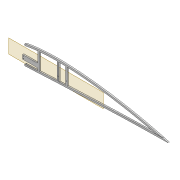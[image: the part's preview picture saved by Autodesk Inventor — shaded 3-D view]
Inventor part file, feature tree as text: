
AUTODESK INVENTOR PART (.ipt)
format: ipt  version: 2022 (Build 260153000, 153)  size: 449,536 bytes
history: native  units: mm
features: extrude x8, sketch x7, projected_geometry x6, fillet x2, shell x1, plane x1
ambient origin geometry x8: Origin, YZ Plane, XZ Plane, XY Plane, X Axis, Y Axis, Z Axis, Center Point
bodies: Solid1 (feature_tree)
feature tree (25):
  extrude  "Extrusion1"  Depth=5.0mm
  shell  "Shell1"  Thickness=2.0mm
  extrude  "Extrusion8"  Depth=5.9mm
  extrude  "Extrusion3"  Depth=10.0mm TaperAngle=0.0deg
  extrude  "Extrusion4"  Depth=2.0mm
  fillet  "Fillet1"  Radius=5.0mm
  sketch  "Sketch10"  dims[d22=4.0mm d23=0.0mm d31=2.0mm d32=5.0mm]
  extrude  "Extrusion5"  Depth=2.5mm
  plane  "Work Plane2"
  extrude  "Extrusion9"  Depth=1.6mm
  fillet  "Fillet2"  Radius=2.5mm
  extrude  "Extrusion10"  Depth=0.5mm
  extrude  "Extrusion11"  Depth=0.5mm TaperAngle=0.0deg
  sketch  "Sketch3"  dims[d0=4.0mm d1=0.0mm d2=5.0mm d7=2.0mm]
  sketch  "Sketch8"  dims[d8=2.0mm d9=5.9mm]
  sketch  "Sketch9"  dims[d13=10.0mm d14=0.0mm d16=10.0mm d17=0.0mm]
  projected_geometry  "Projected Loop4"
  projected_geometry  "Projected Loop10"
  sketch  "Sketch24"  dims[d34=1.6mm d35=2.5mm]
  projected_geometry  "Projected Loop11"
  projected_geometry  "Projected Loop12"
  projected_geometry  "Projected Loop13"
  sketch  "Sketch26"  dims[d37=5.0mm d38=1.6mm d40=2.5mm]
  projected_geometry  "Projected Loop14"
  sketch  "Sketch27"  dims[d62=80.0mm d63=6.0mm d64=4.0mm d65=0.0mm d66=3.0mm d67=12.0mm d68=5.0mm d69=45.0mm d70=12.0mm d71=3.05mm d72=10.0mm d73=0.0mm d74=2.0mm d75=100.0mm d76=20.0mm d77=0.5mm d78=10.0mm d79=0.0mm d80=10.0mm d81=0.0mm]
